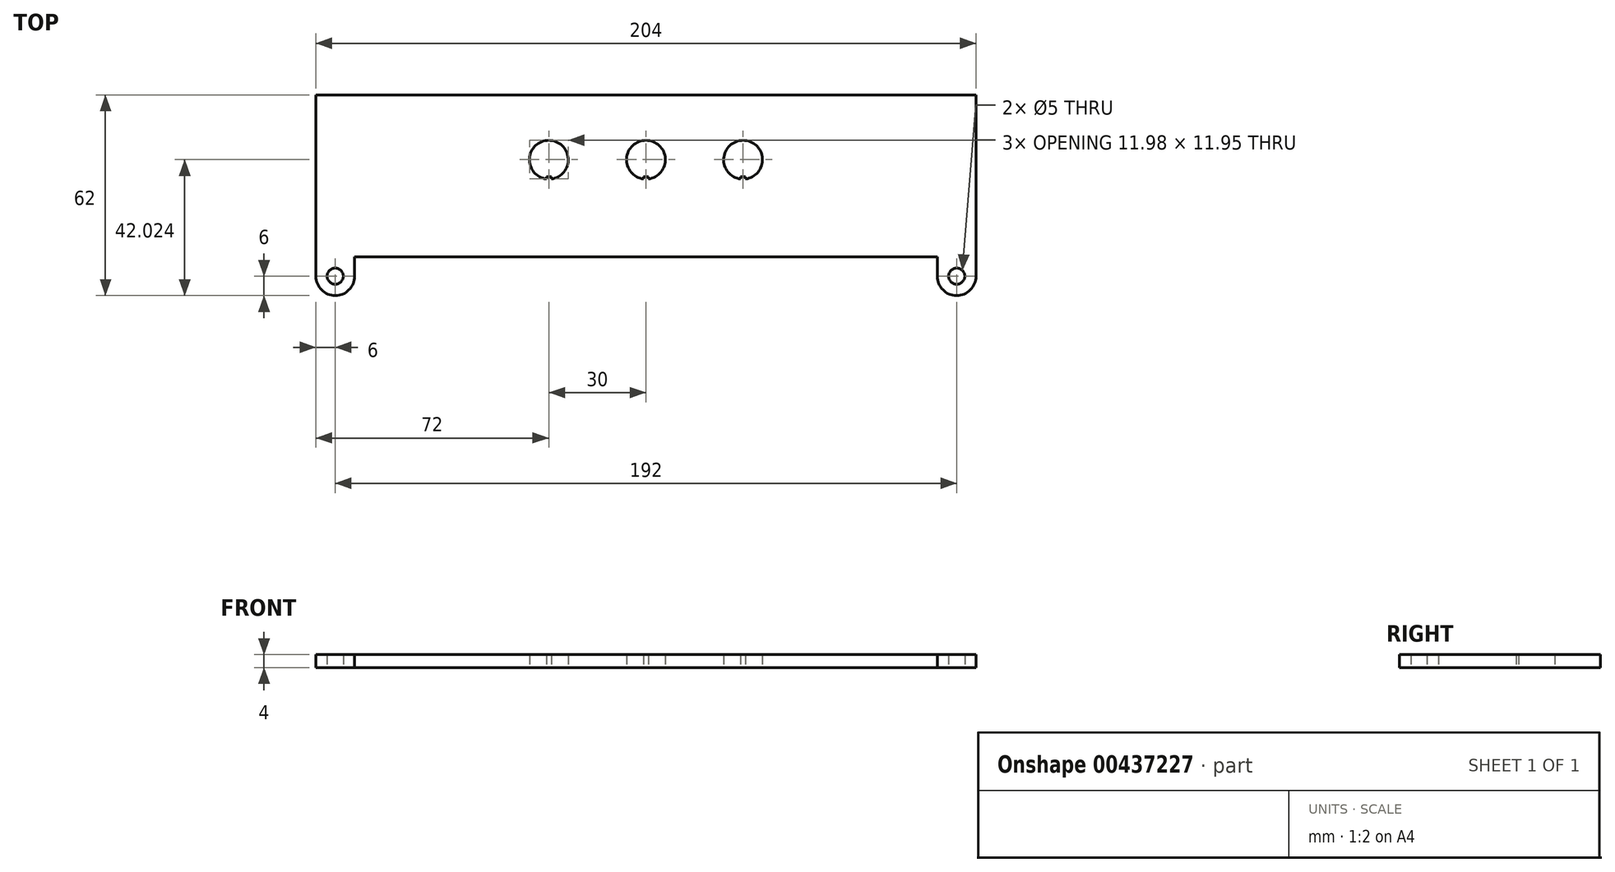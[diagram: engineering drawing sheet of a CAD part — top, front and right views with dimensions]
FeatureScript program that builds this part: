
annotation { "Feature Type Name" : "Feature", "Feature Type Description" : "" }
export const myFeature = defineFeature(function(context is Context, id is Id, definition is map)
    precondition{}
    {
        {
            var Q0;
            Q0=qCreatedBy(makeId("Top.planeOp"),FACE);
            var sketch = newSketch(context, id + "F0", { "sketchPlane" : qUnion([Q0])});
            skLineSegment(sketch, "E0.bottom", {"start": v(-102, 25) * mm, "end": v(102, 25) * mm});
            skLineSegment(sketch, "E0.top", {"start": v(-90, -25) * mm, "end": v(90, -25) * mm});
            skLineSegment(sketch, "E0.left", {"start": v(-102, 25) * mm, "end": v(-102, -25) * mm});
            skLineSegment(sketch, "E0.right", {"start": v(102, 25) * mm, "end": v(102, -25) * mm});
            skPoint(sketch, "E0.middle", {"position": v(0, 0) * mm});
            skArc(sketch, "E1", {"start": v(-102, -31) * mm, "mid": v(-96, -37) * mm, "end": v(-90, -31) * mm});
            skArc(sketch, "E2", {"start": v(90, -31) * mm, "mid": v(96, -37) * mm, "end": v(102, -31) * mm});
            skLineSegment(sketch, "E3", {"start": v(-102, -25) * mm, "end": v(-102, -31) * mm});
            skLineSegment(sketch, "E4", {"start": v(-90, -31) * mm, "end": v(-90, -25) * mm});
            skLineSegment(sketch, "E5", {"start": v(102, -25) * mm, "end": v(102, -31) * mm});
            skLineSegment(sketch, "E6", {"start": v(90, -31) * mm, "end": v(90, -25) * mm});
            skCircle(sketch, "E7", {"center": v(96, -31) * mm, "radius": 2.5 * mm});
            skCircle(sketch, "E8", {"center": v(-96, -31) * mm, "radius": 2.5 * mm});
            skArc(sketch, "E9", {"start": v(-29.25, -0.95) * mm, "mid": v(-30, 11) * mm, "end": v(-30.75, -0.95) * mm});
            skCircle(sketch, "E10", {"center": v(0, 5) * mm, "radius": 6 * mm});
            skCircle(sketch, "E11", {"center": v(30, 5) * mm, "radius": 6 * mm});
            skLineSegment(sketch, "E12", {"start": v(-30.75, -0.95) * mm, "end": v(-30.75, -0.2) * mm});
            skLineSegment(sketch, "E13", {"start": v(-30.75, -0.2) * mm, "end": v(-29.25, -0.2) * mm});
            skLineSegment(sketch, "E14", {"start": v(-29.25, -0.2) * mm, "end": v(-29.25, -0.95) * mm});
            skLineSegment(sketch, "E15", {"start": v(-0.75, -0.95) * mm, "end": v(-0.75, -0.2) * mm});
            skLineSegment(sketch, "E16", {"start": v(-0.75, -0.2) * mm, "end": v(0.75, -0.2) * mm});
            skLineSegment(sketch, "E17", {"start": v(0.75, -0.2) * mm, "end": v(0.75, -0.95) * mm});
            skLineSegment(sketch, "E18", {"start": v(29.25, -0.95) * mm, "end": v(29.25, -0.2) * mm});
            skLineSegment(sketch, "E19", {"start": v(29.25, -0.2) * mm, "end": v(30.75, -0.2) * mm});
            skLineSegment(sketch, "E20", {"start": v(30.75, -0.2) * mm, "end": v(30.75, -0.95) * mm});
            skSolve(sketch);
        }
        {
            var Q0;
            Q0=makeQuery(id+"F0.imprint","IMPRINT",FACE,{"disambiguationData":[TD([[makeQuery(id+"F0.imprint","IMPRINT",EDGE,{"derivedFrom":sQuery(id+"F0.wireOp",EDGE,"E0.bottom")}),-1.0]])]});
            var Q1;
            {var subQ0=sQuery(id+"F0.wireOp",EDGE,"E15");Q1=makeQuery(id+"F0.imprint","IMPRINT",FACE,{"disambiguationData":[TD([[makeQuery(id+"F0.imprint","IMPRINT",EDGE,{"derivedFrom":subQ0}),-1.0]])]});}
            var Q2;
            {var subQ0=sQuery(id+"F0.wireOp",EDGE,"E18");Q2=makeQuery(id+"F0.imprint","IMPRINT",FACE,{"disambiguationData":[TD([[makeQuery(id+"F0.imprint","IMPRINT",EDGE,{"derivedFrom":subQ0}),-1.0]])]});}
            extrude(context, id + "F1", {"entities" : qUnion([Q0, Q1, Q2]), "depth" : 4 * mm});
        }
    });
